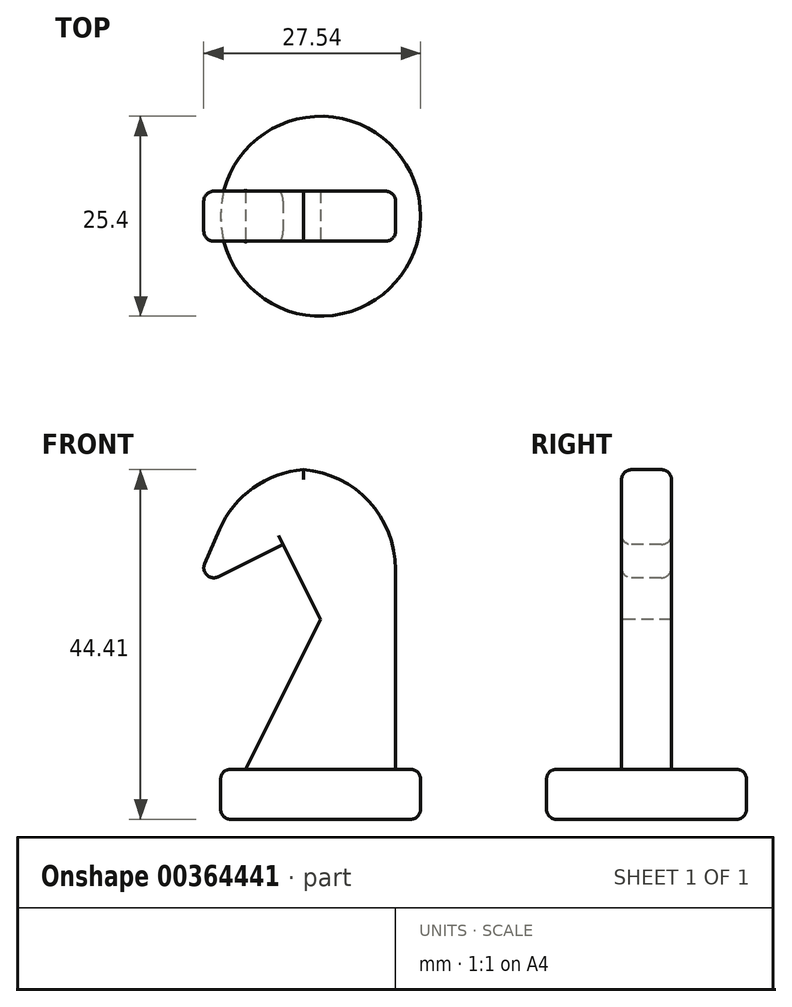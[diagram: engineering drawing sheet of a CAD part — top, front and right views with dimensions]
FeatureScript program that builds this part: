
annotation { "Feature Type Name" : "Feature", "Feature Type Description" : "" }
export const myFeature = defineFeature(function(context is Context, id is Id, definition is map)
    precondition{}
    {
        {
            var Q0;
            Q0=qCreatedBy(makeId("Top.planeOp"),FACE);
            var sketch = newSketch(context, id + "F0", { "sketchPlane" : qUnion([Q0])});
            skCircle(sketch, "E0", {"center": v(0, 0) * mm, "radius": 12.7 * mm});
            skSolve(sketch);
        }
        {
            var Q0;
            Q0 = qSketchRegion(id + "F0", true);
            extrude(context, id + "F1", {"entities" : qUnion([Q0]), "depth" : 6.35 * mm});
        }
        {
            var Q0;
            Q0=makeQuery(id+"F1.opExtrude","CAP_FACE",FACE,{"disambiguationData":[OSD([sQuery(id+"F0.wireOp",EDGE,"E0")])],"isStart":false});
            var sketch = newSketch(context, id + "F2", { "sketchPlane" : qUnion([Q0])});
            skLineSegment(sketch, "E1.bottom", {"start": v(-9.53, 3.17) * mm, "end": v(9.52, 3.18) * mm});
            skLineSegment(sketch, "E1.top", {"start": v(-9.53, -3.18) * mm, "end": v(9.53, -3.18) * mm});
            skLineSegment(sketch, "E1.left", {"start": v(-9.53, 3.17) * mm, "end": v(-9.52, -3.18) * mm});
            skLineSegment(sketch, "E1.right", {"start": v(9.52, 3.18) * mm, "end": v(9.53, -3.17) * mm});
            skPoint(sketch, "E1.middle", {"position": v(0, 0) * mm});
            skSolve(sketch);
        }
        {
            var Q0;
            Q0 = qSketchRegion(id + "F2", true);
            extrude(context, id + "F3", {"entities" : qUnion([Q0]), "operationType" : NewBodyOperationType.ADD, "depth" : 38.1 * mm});
        }
        {
            var Q0;
            Q0=makeQuery(id+"F3.opExtrude","SWEPT_FACE",FACE,{"disambiguationData":[OSD([sQuery(id+"F2.wireOp",EDGE,"E1.top")])]});
            var sketch = newSketch(context, id + "F4", { "sketchPlane" : qUnion([Q0])});
            skLineSegment(sketch, "E2", {"start": v(-9.52, 25.4) * mm, "end": v(0, 25.4) * mm});
            skLineSegment(sketch, "E3", {"start": v(0, 25.4) * mm, "end": v(-9.52, 6.35) * mm});
            skLineSegment(sketch, "E4", {"start": v(0, 25.4) * mm, "end": v(-9.52, 44.45) * mm});
            skSolve(sketch);
        }
        {
            var Q0;
            {var subQ0=sQuery(id+"F4.wireOp",EDGE,"E2");Q0=makeQuery(id+"F4.imprint","IMPRINT",FACE,{"disambiguationData":[TD([[makeQuery(id+"F4.imprint","IMPRINT",EDGE,{"derivedFrom":subQ0}),1.0]])]});}
            var Q1;
            {var subQ0=sQuery(id+"F4.wireOp",EDGE,"E2");Q1=makeQuery(id+"F4.imprint","IMPRINT",FACE,{"disambiguationData":[TD([[makeQuery(id+"F4.imprint","IMPRINT",EDGE,{"derivedFrom":subQ0}),-1.0]])]});}
            extrude(context, id + "F5", {"entities" : qUnion([Q0, Q1]), "operationType" : NewBodyOperationType.REMOVE, "endBound" : BoundingType.UP_TO_NEXT, "oppositeDirection" : true, "depth" : 25.4 * mm});
        }
        {
            var Q0;
            Q0=makeQuery(id+"F5.boolean.opBoolean","COPY",FACE,{"derivedFrom":makeQuery(id+"F5.opExtrude","SWEPT_FACE",FACE,{"disambiguationData":[OSD([sQuery(id+"F4.wireOp",EDGE,"E4")])]})});
            var sketch = newSketch(context, id + "F6", { "sketchPlane" : qUnion([Q0])});
            skLineSegment(sketch, "E5.bottom", {"start": v(-3.17, 44.02) * mm, "end": v(3.18, 44.02) * mm});
            skLineSegment(sketch, "E5.top", {"start": v(-3.17, 33.37) * mm, "end": v(3.18, 33.37) * mm});
            skLineSegment(sketch, "E5.left", {"start": v(-3.17, 44.02) * mm, "end": v(-3.17, 33.37) * mm});
            skLineSegment(sketch, "E5.right", {"start": v(3.18, 44.02) * mm, "end": v(3.18, 33.37) * mm});
            skSolve(sketch);
        }
        {
            var Q0;
            Q0 = qSketchRegion(id + "F6", true);
            extrude(context, id + "F7", {"entities" : qUnion([Q0]), "operationType" : NewBodyOperationType.ADD, "depth" : 12.7 * mm});
        }
        {
            var Q0;
            Q0=makeQuery(id+"F7.boolean.opBoolean","MERGE",FACE,{"derivedFrom":[makeQuery(id+"F3.opExtrude","SWEPT_FACE",FACE,{"disambiguationData":[OSD([sQuery(id+"F2.wireOp",EDGE,"E1.top")])]}),makeQuery(id+"F7.opExtrude","SWEPT_FACE",FACE,{"disambiguationData":[OSD([sQuery(id+"F6.wireOp",EDGE,"E5.right")])]})]});
            var sketch = newSketch(context, id + "F8", { "sketchPlane" : qUnion([Q0])});
            skLineSegment(sketch, "E6", {"start": v(-16.12, 29.25) * mm, "end": v(-9.52, 44.45) * mm});
            skSolve(sketch);
        }
        {
            var Q0;
            Q0=makeQuery(id+"F8.imprint","IMPRINT",FACE,{"disambiguationData":[TD([[makeQuery(id+"F8.imprint","IMPRINT",EDGE,{"derivedFrom":sQuery(id+"F8.wireOp",EDGE,"E6")}),1.0]])]});
            extrude(context, id + "F9", {"entities" : qUnion([Q0]), "operationType" : NewBodyOperationType.REMOVE, "endBound" : BoundingType.UP_TO_NEXT, "oppositeDirection" : true, "depth" : 25.4 * mm});
        }
        {
            var Q0;
            {var subQ0=sQuery(id+"F6.wireOp",EDGE,"E5.bottom");var subQ1=sQuery(id+"F2.wireOp",EDGE,"E1.left");Q0=makeQuery(id+"F9.boolean.opBoolean","MERGE",EDGE,{"derivedFrom":[makeQuery(id+"F7.boolean.opBoolean","MERGE",EDGE,{"derivedFrom":[makeQuery(id+"F5.boolean.opBoolean","MERGE",EDGE,{"derivedFrom":[makeQuery(id+"F3.opExtrude","CAP_EDGE",EDGE,{"disambiguationData":[OSD([subQ1])],"isStart":false})],"fromTools":[makeQuery(id+"F5.opExtrude","SWEPT_EDGE",EDGE,{"disambiguationData":[OSD([sQuery(id+"F2.wireOp",EDGE,"E1.bottom"),subQ1])]})]}),makeQuery(id+"F7.opExtrude","CAP_EDGE",EDGE,{"disambiguationData":[OSD([subQ0])],"isStart":true})]})],"fromTools":[makeQuery(id+"F9.opExtrude","SWEPT_EDGE",EDGE,{"disambiguationData":[OSD([sQuery(id+"F2.wireOp",EDGE,"E1.top"),subQ1,sQuery(id+"F4.wireOp",EDGE,"E4"),subQ0,sQuery(id+"F6.wireOp",EDGE,"E5.right"),sQuery(id+"F8.wireOp",EDGE,"E6")])]})]});}
            var Q1;
            Q1=makeQuery(id+"F3.opExtrude","CAP_EDGE",EDGE,{"disambiguationData":[OSD([sQuery(id+"F2.wireOp",EDGE,"E1.right")])],"isStart":false});
            fillet(context, id + "F10", {"entities" : qUnion([Q0, Q1]), "radius" : 12.7 * mm, "tangentPropagation" : true, "allowEdgeOverflow" : false});
        }
        {
            var Q0;
            Q0=makeQuery(id+"F1.opExtrude","CAP_EDGE",EDGE,{"disambiguationData":[OSD([sQuery(id+"F0.wireOp",EDGE,"E0")])],"isStart":false});
            var Q1;
            Q1=makeQuery(id+"F1.opExtrude","CAP_EDGE",EDGE,{"disambiguationData":[OSD([sQuery(id+"F0.wireOp",EDGE,"E0")])],"isStart":true});
            fillet(context, id + "F11", {"entities" : qUnion([Q0, Q1]), "radius" : 1.27 * mm, "tangentPropagation" : true, "allowEdgeOverflow" : false});
        }
        {
            var Q0;
            Q0=makeQuery(id+"F3.opExtrude","SWEPT_EDGE",EDGE,{"disambiguationData":[OSD([sQuery(id+"F2.wireOp",EDGE,"E1.top"),sQuery(id+"F2.wireOp",EDGE,"E1.right")])]});
            var Q1;
            Q1=makeQuery(id+"F10.opFillet","BLEND_EDGE",EDGE,{"blendedFrom":[makeQuery(id+"F3.opExtrude","CAP_EDGE",EDGE,{"disambiguationData":[OSD([sQuery(id+"F2.wireOp",EDGE,"E1.right")])],"isStart":false}),makeQuery(id+"F7.boolean.opBoolean","MERGE",FACE,{"derivedFrom":[makeQuery(id+"F3.opExtrude","SWEPT_FACE",FACE,{"disambiguationData":[OSD([sQuery(id+"F2.wireOp",EDGE,"E1.top")])]}),makeQuery(id+"F7.opExtrude","SWEPT_FACE",FACE,{"disambiguationData":[OSD([sQuery(id+"F6.wireOp",EDGE,"E5.right")])]})]})],"blendedInto":[makeQuery(id+"F7.boolean.opBoolean","MERGE",FACE,{"derivedFrom":[makeQuery(id+"F3.opExtrude","SWEPT_FACE",FACE,{"disambiguationData":[OSD([sQuery(id+"F2.wireOp",EDGE,"E1.top")])]}),makeQuery(id+"F7.opExtrude","SWEPT_FACE",FACE,{"disambiguationData":[OSD([sQuery(id+"F6.wireOp",EDGE,"E5.right")])]})]})]});
            var Q2;
            {var subQ0=sQuery(id+"F6.wireOp",EDGE,"E5.right");var subQ1=sQuery(id+"F2.wireOp",EDGE,"E1.top");var subQ2=sQuery(id+"F6.wireOp",EDGE,"E5.bottom");var subQ3=sQuery(id+"F2.wireOp",EDGE,"E1.left");Q2=makeQuery(id+"F10.opFillet","BLEND_EDGE",EDGE,{"blendedFrom":[makeQuery(id+"F9.boolean.opBoolean","MERGE",EDGE,{"derivedFrom":[makeQuery(id+"F7.boolean.opBoolean","MERGE",EDGE,{"derivedFrom":[makeQuery(id+"F5.boolean.opBoolean","MERGE",EDGE,{"derivedFrom":[makeQuery(id+"F3.opExtrude","CAP_EDGE",EDGE,{"disambiguationData":[OSD([subQ3])],"isStart":false})],"fromTools":[makeQuery(id+"F5.opExtrude","SWEPT_EDGE",EDGE,{"disambiguationData":[OSD([sQuery(id+"F2.wireOp",EDGE,"E1.bottom"),subQ3])]})]}),makeQuery(id+"F7.opExtrude","CAP_EDGE",EDGE,{"disambiguationData":[OSD([subQ2])],"isStart":true})]})],"fromTools":[makeQuery(id+"F9.opExtrude","SWEPT_EDGE",EDGE,{"disambiguationData":[OSD([subQ1,subQ3,sQuery(id+"F4.wireOp",EDGE,"E4"),subQ2,subQ0,sQuery(id+"F8.wireOp",EDGE,"E6")])]})]}),makeQuery(id+"F7.boolean.opBoolean","MERGE",FACE,{"derivedFrom":[makeQuery(id+"F3.opExtrude","SWEPT_FACE",FACE,{"disambiguationData":[OSD([subQ1])]}),makeQuery(id+"F7.opExtrude","SWEPT_FACE",FACE,{"disambiguationData":[OSD([subQ0])]})]})],"blendedInto":[makeQuery(id+"F7.boolean.opBoolean","MERGE",FACE,{"derivedFrom":[makeQuery(id+"F3.opExtrude","SWEPT_FACE",FACE,{"disambiguationData":[OSD([subQ1])]}),makeQuery(id+"F7.opExtrude","SWEPT_FACE",FACE,{"disambiguationData":[OSD([subQ0])]})]})]});}
            var Q3;
            Q3=makeQuery(id+"F9.boolean.opBoolean","COPY",EDGE,{"derivedFrom":makeQuery(id+"F9.opExtrude","CAP_EDGE",EDGE,{"disambiguationData":[OSD([sQuery(id+"F8.wireOp",EDGE,"E6")])],"isStart":true})});
            var Q4;
            Q4=makeQuery(id+"F7.opExtrude","SWEPT_EDGE",EDGE,{"disambiguationData":[OSD([sQuery(id+"F4.wireOp",EDGE,"E4"),sQuery(id+"F6.wireOp",EDGE,"E5.top"),sQuery(id+"F6.wireOp",EDGE,"E5.right")])]});
            var Q5;
            Q5=makeQuery(id+"F5.boolean.opBoolean","COPY",EDGE,{"derivedFrom":makeQuery(id+"F5.opExtrude","CAP_EDGE",EDGE,{"disambiguationData":[OSD([sQuery(id+"F4.wireOp",EDGE,"E4")])],"isStart":true})});
            var Q6;
            Q6=makeQuery(id+"F5.boolean.opBoolean","COPY",EDGE,{"derivedFrom":makeQuery(id+"F5.opExtrude","CAP_EDGE",EDGE,{"disambiguationData":[OSD([sQuery(id+"F4.wireOp",EDGE,"E3")])],"isStart":true})});
            var Q7;
            {var subQ0=sQuery(id+"F2.wireOp",EDGE,"E1.bottom");var subQ1=sQuery(id+"F6.wireOp",EDGE,"E5.bottom");var subQ2=sQuery(id+"F2.wireOp",EDGE,"E1.left");Q7=makeQuery(id+"F10.opFillet","BLEND_EDGE",EDGE,{"blendedFrom":[makeQuery(id+"F9.boolean.opBoolean","MERGE",EDGE,{"derivedFrom":[makeQuery(id+"F7.boolean.opBoolean","MERGE",EDGE,{"derivedFrom":[makeQuery(id+"F5.boolean.opBoolean","MERGE",EDGE,{"derivedFrom":[makeQuery(id+"F3.opExtrude","CAP_EDGE",EDGE,{"disambiguationData":[OSD([subQ2])],"isStart":false})],"fromTools":[makeQuery(id+"F5.opExtrude","SWEPT_EDGE",EDGE,{"disambiguationData":[OSD([subQ0,subQ2])]})]}),makeQuery(id+"F7.opExtrude","CAP_EDGE",EDGE,{"disambiguationData":[OSD([subQ1])],"isStart":true})]})],"fromTools":[makeQuery(id+"F9.opExtrude","SWEPT_EDGE",EDGE,{"disambiguationData":[OSD([sQuery(id+"F2.wireOp",EDGE,"E1.top"),subQ2,sQuery(id+"F4.wireOp",EDGE,"E4"),subQ1,sQuery(id+"F6.wireOp",EDGE,"E5.right"),sQuery(id+"F8.wireOp",EDGE,"E6")])]})]}),makeQuery(id+"F7.boolean.opBoolean","MERGE",FACE,{"derivedFrom":[makeQuery(id+"F3.opExtrude","SWEPT_FACE",FACE,{"disambiguationData":[OSD([subQ0])]}),makeQuery(id+"F7.opExtrude","SWEPT_FACE",FACE,{"disambiguationData":[OSD([sQuery(id+"F6.wireOp",EDGE,"E5.left")])]})]})],"blendedInto":[makeQuery(id+"F7.boolean.opBoolean","MERGE",FACE,{"derivedFrom":[makeQuery(id+"F3.opExtrude","SWEPT_FACE",FACE,{"disambiguationData":[OSD([subQ0])]}),makeQuery(id+"F7.opExtrude","SWEPT_FACE",FACE,{"disambiguationData":[OSD([sQuery(id+"F6.wireOp",EDGE,"E5.left")])]})]})]});}
            var Q8;
            Q8=makeQuery(id+"F9.boolean.opBoolean","COPY",EDGE,{"derivedFrom":makeQuery(id+"F9.opExtrude","TWEAK_EDGE",EDGE,{"derivedFrom":[makeQuery(id+"F7.boolean.opBoolean","MERGE",FACE,{"derivedFrom":[makeQuery(id+"F3.opExtrude","SWEPT_FACE",FACE,{"disambiguationData":[OSD([sQuery(id+"F2.wireOp",EDGE,"E1.bottom")])]}),makeQuery(id+"F7.opExtrude","SWEPT_FACE",FACE,{"disambiguationData":[OSD([sQuery(id+"F6.wireOp",EDGE,"E5.left")])]})]}),makeQuery(id+"F8.imprint","IMPRINT",EDGE,{"derivedFrom":sQuery(id+"F8.wireOp",EDGE,"E6")})]})});
            var Q9;
            Q9=makeQuery(id+"F7.opExtrude","SWEPT_EDGE",EDGE,{"disambiguationData":[OSD([sQuery(id+"F2.wireOp",EDGE,"E1.bottom"),sQuery(id+"F4.wireOp",EDGE,"E4"),sQuery(id+"F6.wireOp",EDGE,"E5.top"),sQuery(id+"F6.wireOp",EDGE,"E5.left")])]});
            var Q10;
            Q10=makeQuery(id+"F10.opFillet","BLEND_EDGE",EDGE,{"blendedFrom":[makeQuery(id+"F3.opExtrude","CAP_EDGE",EDGE,{"disambiguationData":[OSD([sQuery(id+"F2.wireOp",EDGE,"E1.right")])],"isStart":false}),makeQuery(id+"F7.boolean.opBoolean","MERGE",FACE,{"derivedFrom":[makeQuery(id+"F3.opExtrude","SWEPT_FACE",FACE,{"disambiguationData":[OSD([sQuery(id+"F2.wireOp",EDGE,"E1.bottom")])]}),makeQuery(id+"F7.opExtrude","SWEPT_FACE",FACE,{"disambiguationData":[OSD([sQuery(id+"F6.wireOp",EDGE,"E5.left")])]})]})],"blendedInto":[makeQuery(id+"F7.boolean.opBoolean","MERGE",FACE,{"derivedFrom":[makeQuery(id+"F3.opExtrude","SWEPT_FACE",FACE,{"disambiguationData":[OSD([sQuery(id+"F2.wireOp",EDGE,"E1.bottom")])]}),makeQuery(id+"F7.opExtrude","SWEPT_FACE",FACE,{"disambiguationData":[OSD([sQuery(id+"F6.wireOp",EDGE,"E5.left")])]})]})]});
            var Q11;
            Q11=makeQuery(id+"F3.opExtrude","SWEPT_EDGE",EDGE,{"disambiguationData":[OSD([sQuery(id+"F2.wireOp",EDGE,"E1.bottom"),sQuery(id+"F2.wireOp",EDGE,"E1.right")])]});
            var Q12;
            Q12=makeQuery(id+"F5.boolean.opBoolean","COPY",EDGE,{"derivedFrom":makeQuery(id+"F5.opExtrude","TWEAK_EDGE",EDGE,{"derivedFrom":[makeQuery(id+"F3.opExtrude","SWEPT_FACE",FACE,{"disambiguationData":[OSD([sQuery(id+"F2.wireOp",EDGE,"E1.bottom")])]}),makeQuery(id+"F4.imprint","IMPRINT",EDGE,{"derivedFrom":sQuery(id+"F4.wireOp",EDGE,"E4")})]})});
            var Q13;
            Q13=makeQuery(id+"F5.boolean.opBoolean","COPY",EDGE,{"derivedFrom":makeQuery(id+"F5.opExtrude","CAP_EDGE",EDGE,{"disambiguationData":[OSD([sQuery(id+"F4.wireOp",EDGE,"E3")])],"isStart":false})});
            var Q14;
            {var subQ0=sQuery(id+"F6.wireOp",EDGE,"E5.top");Q14=makeQuery(id+"F9.boolean.opBoolean","MERGE",EDGE,{"derivedFrom":[makeQuery(id+"F7.opExtrude","CAP_EDGE",EDGE,{"disambiguationData":[OSD([subQ0])],"isStart":false})],"fromTools":[makeQuery(id+"F9.opExtrude","SWEPT_EDGE",EDGE,{"disambiguationData":[OSD([sQuery(id+"F2.wireOp",EDGE,"E1.bottom"),sQuery(id+"F4.wireOp",EDGE,"E4"),subQ0,sQuery(id+"F6.wireOp",EDGE,"E5.left")])]})]});}
            fillet(context, id + "F12", {"entities" : qUnion([Q0, Q1, Q2, Q3, Q4, Q5, Q6, Q7, Q8, Q9, Q10, Q11, Q12, Q13, Q14]), "radius" : 1.27 * mm, "tangentPropagation" : true, "allowEdgeOverflow" : false});
        }
        {
            var Q0;
            Q0=makeQuery(id+"F3.opExtrude","CAP_EDGE",EDGE,{"disambiguationData":[OSD([sQuery(id+"F2.wireOp",EDGE,"E1.top")])],"isStart":true});
            var Q1;
            Q1=makeQuery(id+"F12.opFillet","BLEND_EDGE",EDGE,{"blendedFrom":[makeQuery(id+"F3.opExtrude","SWEPT_EDGE",EDGE,{"disambiguationData":[OSD([sQuery(id+"F2.wireOp",EDGE,"E1.top"),sQuery(id+"F2.wireOp",EDGE,"E1.right")])]}),makeQuery(id+"F1.opExtrude","CAP_FACE",FACE,{"disambiguationData":[OSD([sQuery(id+"F0.wireOp",EDGE,"E0")])],"isStart":false})],"blendedInto":[makeQuery(id+"F1.opExtrude","CAP_FACE",FACE,{"disambiguationData":[OSD([sQuery(id+"F0.wireOp",EDGE,"E0")])],"isStart":false})]});
            fillet(context, id + "F13", {"entities" : qUnion([Q0, Q1]), "radius" : 0.25 * mm, "tangentPropagation" : true, "allowEdgeOverflow" : false});
        }
    });
